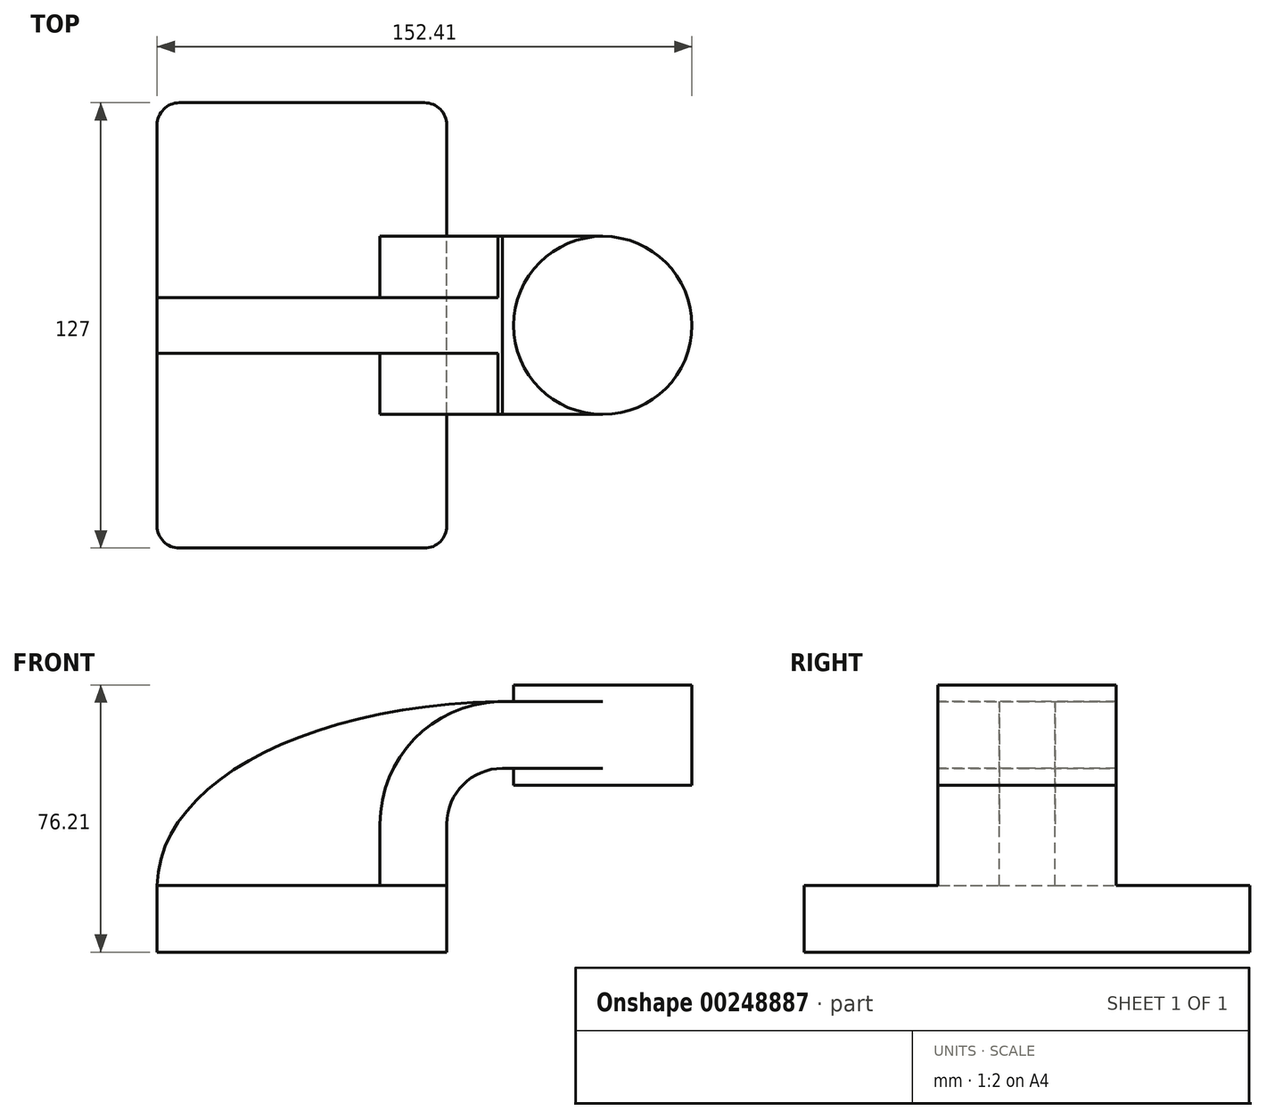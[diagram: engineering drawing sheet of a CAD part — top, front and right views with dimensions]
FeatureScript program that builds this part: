
annotation { "Feature Type Name" : "Feature", "Feature Type Description" : "" }
export const myFeature = defineFeature(function(context is Context, id is Id, definition is map)
    precondition{}
    {
        {
            var Q0;
            Q0=qCreatedBy(makeId("Front.planeOp"),FACE);
            var sketch = newSketch(context, id + "F0", { "sketchPlane" : qUnion([Q0])});
            skLineSegment(sketch, "E0.bottom", {"start": v(-41.28, -9.53) * mm, "end": v(41.28, -9.53) * mm});
            skLineSegment(sketch, "E0.top", {"start": v(-41.28, 9.52) * mm, "end": v(41.28, 9.52) * mm});
            skLineSegment(sketch, "E0.left", {"start": v(-41.27, -9.53) * mm, "end": v(-41.28, 9.52) * mm});
            skLineSegment(sketch, "E0.right", {"start": v(41.28, -9.53) * mm, "end": v(41.28, 9.52) * mm});
            skPoint(sketch, "E0.middle", {"position": v(0, 0) * mm});
            skLineSegment(sketch, "E1.bottom", {"start": v(60.32, 38.1) * mm, "end": v(111.12, 38.1) * mm});
            skLineSegment(sketch, "E1.top", {"start": v(60.32, 66.67) * mm, "end": v(111.12, 66.67) * mm});
            skLineSegment(sketch, "E1.left", {"start": v(60.32, 38.1) * mm, "end": v(60.32, 66.67) * mm});
            skLineSegment(sketch, "E1.right", {"start": v(111.12, 38.1) * mm, "end": v(111.12, 66.67) * mm});
            skPoint(sketch, "E1.middle", {"position": v(85.72, 52.39) * mm});
            skLineSegment(sketch, "E2", {"start": v(41.27, 9.52) * mm, "end": v(41.27, 27) * mm});
            skArc(sketch, "E3", {"start": v(41.27, 27) * mm, "mid": v(45.92, 38.23) * mm, "end": v(57.15, 42.88) * mm});
            skLineSegment(sketch, "E4", {"start": v(57.15, 42.88) * mm, "end": v(85.72, 42.88) * mm});
            skPoint(sketch, "E4.endSnap0", {"position": v(85.72, 38.1) * mm});
            skLineSegment(sketch, "E5.0", {"start": v(57.15, 61.93) * mm, "end": v(85.72, 61.93) * mm});
            skArc(sketch, "E5.1", {"start": v(22.22, 27) * mm, "mid": v(32.45, 51.7) * mm, "end": v(57.15, 61.93) * mm});
            skLineSegment(sketch, "E5.2", {"start": v(22.22, 9.52) * mm, "end": v(22.22, 27) * mm});
            skFitSpline(sketch, "E6", {"points": [v(-41.28, 9.52) * mm, v(57.15, 61.93) * mm], "startDerivative": vector(2.06, 88.67) * mm, "endDerivative": vector(165.86, 2.63) * mm});
            skLineSegment(sketch, "E7", {"start": v(85.72, 38.1) * mm, "end": v(85.72, 66.67) * mm});
            skSolve(sketch);
        }
        {
            var Q0;
            Q0=makeQuery(id+"F0.imprint","IMPRINT",FACE,{"disambiguationData":[TD([[makeQuery(id+"F0.imprint","IMPRINT",EDGE,{"derivedFrom":sQuery(id+"F0.wireOp",EDGE,"E0.bottom")}),1.0]])]});
            extrude(context, id + "F1", {"entities" : qUnion([Q0]), "endBound" : BoundingType.SYMMETRIC, "depth" : 127 * mm});
        }
        {
            var Q0;
            {var subQ1=sQuery(id+"F0.wireOp",EDGE,"E2");Q0=makeQuery(id+"F0.imprint","IMPRINT",FACE,{"disambiguationData":[TD([[makeQuery(id+"F0.imprint","IMPRINT",EDGE,{"derivedFrom":subQ1}),1.0]])]});}
            var Q1;
            {var subQ0=sQuery(id+"F0.wireOp",EDGE,"E4");var subQ1=sQuery(id+"F0.wireOp",EDGE,"E1.left");var subQ2=makeQuery(id+"F0.imprint","INTERSECT",VERTEX,{"derivedFrom":[subQ1,subQ0]});Q1=makeQuery(id+"F0.imprint","IMPRINT",FACE,{"disambiguationData":[TD([[makeQuery(id+"F0.imprint","IMPRINT",EDGE,{"disambiguationData":[TD([[subQ2,-1.0]])],"derivedFrom":subQ1}),-1.0]])]});}
            extrude(context, id + "F2", {"entities" : qUnion([Q0, Q1]), "operationType" : NewBodyOperationType.ADD, "endBound" : BoundingType.SYMMETRIC, "depth" : 50.8 * mm});
        }
        {
            var Q0;
            {var subQ3=sQuery(id+"F0.wireOp",EDGE,"E5.2");Q0=makeQuery(id+"F0.imprint","IMPRINT",FACE,{"disambiguationData":[TD([[makeQuery(id+"F0.imprint","IMPRINT",EDGE,{"derivedFrom":subQ3}),1.0]])]});}
            extrude(context, id + "F3", {"entities" : qUnion([Q0]), "operationType" : NewBodyOperationType.ADD, "endBound" : BoundingType.SYMMETRIC, "depth" : 15.88 * mm});
        }
        {
            var Q0;
            {var subQ0=sQuery(id+"F0.wireOp",EDGE,"E1.right");Q0=makeQuery(id+"F0.imprint","IMPRINT",FACE,{"disambiguationData":[TD([[makeQuery(id+"F0.imprint","IMPRINT",EDGE,{"derivedFrom":subQ0}),1.0]])]});}
            var Q1;
            Q1=sQuery(id+"F0.wireOp",EDGE,"E7");
            revolve(context, id + "F4", {"operationType" : NewBodyOperationType.ADD, "entities" : qUnion([Q0]), "axis" : qUnion([Q1]), "revolveType" : RevolveType.FULL});
        }
        {
            var Q0;
            Q0=makeQuery(id+"F1.opExtrude","CAP_EDGE",EDGE,{"disambiguationData":[OSD([sQuery(id+"F0.wireOp",EDGE,"E0.right")])],"isStart":false});
            var Q1;
            Q1=makeQuery(id+"F1.opExtrude","CAP_EDGE",EDGE,{"disambiguationData":[OSD([sQuery(id+"F0.wireOp",EDGE,"E0.left")])],"isStart":false});
            var Q2;
            Q2=makeQuery(id+"F1.opExtrude","CAP_EDGE",EDGE,{"disambiguationData":[OSD([sQuery(id+"F0.wireOp",EDGE,"E0.left")])],"isStart":true});
            var Q3;
            Q3=makeQuery(id+"F1.opExtrude","CAP_EDGE",EDGE,{"disambiguationData":[OSD([sQuery(id+"F0.wireOp",EDGE,"E0.right")])],"isStart":true});
            fillet(context, id + "F5", {"entities" : qUnion([Q0, Q1, Q2, Q3]), "radius" : 6.35 * mm, "tangentPropagation" : true, "allowEdgeOverflow" : false});
        }
    });
